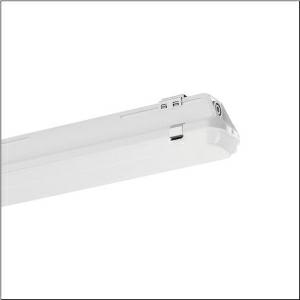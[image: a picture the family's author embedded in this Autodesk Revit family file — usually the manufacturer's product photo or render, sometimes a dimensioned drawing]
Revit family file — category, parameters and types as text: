
# Revit family: monsun_21_51fb107p420c
name_source: partatom
category: Lighting Fixtures
units: mm (PartAtom-declared; Revit-internal decimal feet)

## family parameters
Cut with Voids When Loaded = No
Host = Face
Light Source = No
Part Type = Normal
Room Calculation Point = No
Round Connector Dimension = Use Diameter
Shared = No

## types (1)
- Monsun 21 (1 x LED, 2580 lm, 15.4 W, 4000K)
    Apparent Load = 15 VA
    CIE Flux Codes = 47 77 93 94 100
    Color Rendering = 80
    Color Temperature = 4000K
    Default Elevation = 1800 mm
    Description = Monsun 21, damp-proof luminaire, chain hanger, primary optical cover: enclosure, of PMMA, light emission: direct distribution, primary light characteristic: symmetric, installation type: suspended mounting, surface-mounted, horizontal mounting, vertical mounting, LED, rated luminous flux: 2.580lm, luminous efficacy: 168lm/W, light colour: 840, colour temperature: 4000K, control gear: ON/OFF, with terminal, 3-pole, max. 2.5mm², mains connection: 220..240V, AC, 50/60Hz, rated input power: 15W, housing, of glass-fibre reinforced polyester, uncoated, bright grey, incl. chain hanger, length: 1.590mm, width: 90mm, height: 88mm, clip for enclosure, of stainless steel (V2A), ceiling mounting element, of stainless steel (V2A), chain hanger, of stainless steel (V2A), protection rating (complete): IP66, insulation class (complete): insulation class I (protective earthing), certification: CE, ENEC, VDE, UKCA, protection symbol: D, impact resistance: IK04, permissible operating ambient temperature: -25..+35°C, standard: EN 50419, EN 60598-2-1, corresponds to IFS (International Featured Standards) requirements for safety and quality in the food industry, for indoor or canopied outdoor use, no direct snow, no direct sun, no direct rain, LABS conformity tested according to VDMA 24364:2018-05, contact your sales advisor before using the luminaires in applications with unclear chemical exposure, large temperature fluctuations or condensation-forming humidity, packaging unit: 1 piece
    Height = 89 mm
    Lamp = 1 x LED
    Lamp Light Flux = 2580 lm
    Lamp Power = 15.4 W
    Lamp count = 1
    Length = 1590 mm
    Luminous efficacy = 168 lm/W
    Manufacturer = Siteco
    ModVariant = No
    Model = 51FB107P420C
    Mounting Place = Ceiling
    Mounting Type = Surface mounted
    Number of Poles = 1
    OnlyDefault = Yes
    Power Factor = 1
    Product Name = Monsun 21
    Product group = damp-proof luminaire
    ProductGroupID = 300
    Protection Class = Protection class I
    Protection Degree = IP 66
    RLX_Detail_Level = 1
    RLX_Emergency_Light_Flux = 0 lm
    RLX_Emergency_Type = 0
    RLX_Emergency_Type_DB = No
    RlxData = <blob elided: 88265 chars, md5=582e6d4c>
    Socket = socket
    Standby Power = 0 W
    System Light Flux = 2580 lm
    System Power = 15 W
    Type Comments = Product without accessories
    Type Image = l_1319656.jpg
    URL = http://relux.com
    VarID = ---
    Voltage = 0 V
    Weight = 0.00 kg
    Width = 90 mm

## geometry (parser evidence)
native form markers: Blend x4, Sweep x14
no freeform markers — native parametric forms only
